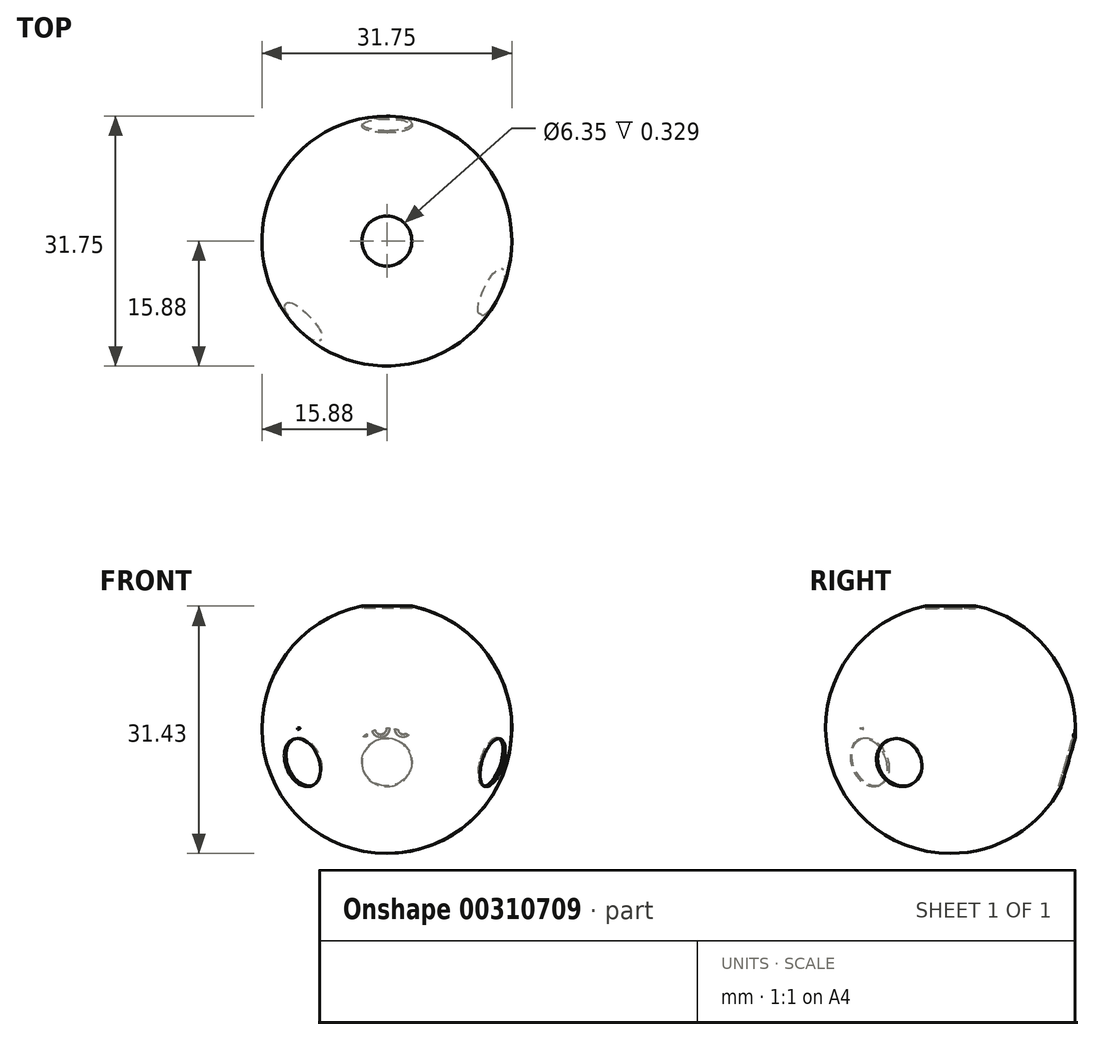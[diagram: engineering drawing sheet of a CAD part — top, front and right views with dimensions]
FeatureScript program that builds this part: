
annotation { "Feature Type Name" : "Feature", "Feature Type Description" : "" }
export const myFeature = defineFeature(function(context is Context, id is Id, definition is map)
    precondition{}
    {
        {
            var Q0;
            Q0=qCreatedBy(makeId("Front.planeOp"),FACE);
            var sketch = newSketch(context, id + "F0", { "sketchPlane" : qUnion([Q0])});
            skArc(sketch, "E0", {"start": v(0, 15.88) * mm, "mid": v(-15.88, 0) * mm, "end": v(0, -15.88) * mm});
            skLineSegment(sketch, "E1", {"start": v(0, 15.88) * mm, "end": v(0, -15.88) * mm});
            skSolve(sketch);
        }
        {
            var Q0;
            Q0=qCreatedBy(makeId("Top.planeOp"),FACE);
            var sketch = newSketch(context, id + "F1", { "sketchPlane" : qUnion([Q0])});
            skCircle(sketch, "E2", {"center": v(0, 0) * mm, "radius": 15.88 * mm});
            skSolve(sketch);
        }
        {
            var Q0;
            Q0=makeQuery(id+"F0.imprint","IMPRINT",FACE,{"disambiguationData":[TD([[makeQuery(id+"F0.imprint","IMPRINT",EDGE,{"derivedFrom":sQuery(id+"F0.wireOp",EDGE,"E0")}),1.0]])]});
            var Q1;
            Q1=sQuery(id+"F1.wireOp",EDGE,"E2");
            revolve(context, id + "F2", {"entities" : qUnion([Q0]), "axis" : qUnion([Q1]), "revolveType" : RevolveType.FULL});
        }
        {
            var Q0;
            Q0=qCreatedBy(makeId("Top.planeOp"),FACE);
            cPlane(context, id + "F3", {"entities" : qUnion([Q0]), "cplaneType" : CPlaneType.OFFSET, "offset" : 15.24 * mm, "width" : 152.4 * mm, "height" : 152.4 * mm});
        }
        {
            var Q0;
            Q0=qCreatedBy(id+"F3.planeOp",FACE);
            cPlane(context, id + "F4", {"entities" : qUnion([Q0]), "cplaneType" : CPlaneType.OFFSET, "offset" : 3 / 203.2 * mm, "oppositeDirection" : true, "width" : 152.4 * mm, "height" : 152.4 * mm});
        }
        {
            var Q0;
            Q0=qCreatedBy(id+"F4.planeOp",FACE);
            var sketch = newSketch(context, id + "F5", { "sketchPlane" : qUnion([Q0])});
            skCircle(sketch, "E3", {"center": v(0, 0) * mm, "radius": 3.18 * mm});
            skSolve(sketch);
        }
        {
            var Q0;
            Q0=qSketchRegion(id+"F5",true);
            extrude(context, id + "F6", {"entities" : qUnion([Q0]), "depth" : 50.8 * mm});
        }
        {
            var Q0;
            Q0=qCreatedBy(makeId("Front.planeOp"),FACE);
            var sketch = newSketch(context, id + "F7", { "sketchPlane" : qUnion([Q0])});
            skLineSegment(sketch, "E4", {"start": v(0, 0) * mm, "end": v(0, -53.82) * mm, "construction": true});
            skLineSegment(sketch, "E5", {"start": v(0, 0) * mm, "end": v(-63.8, 0) * mm, "construction": true});
            skSolve(sketch);
        }
        {
            var Q0;
            Q0=makeQuery(id+"F6.opExtrude","SWEPT_BODY",BODY,{"disambiguationData":[OSD([sQuery(id+"F5.wireOp",EDGE,"E3")])]});
            var Q1;
            Q1=sQuery(id+"F7.wireOp",EDGE,"E5");
            transform(context, id + "F8", {"entities" : qUnion([Q0]), "transformType" : TransformType.ROTATION, "transformAxis" : qUnion([Q1]), "angle" : 106.2 * degree, "makeCopy" : true});
        }
        {
            var Q0;
            Q0=makeQuery(id+"F8.opPattern","COPY",BODY,{"derivedFrom":makeQuery(id+"F6.opExtrude","SWEPT_BODY",BODY,{"disambiguationData":[OSD([sQuery(id+"F5.wireOp",EDGE,"E3")])]}),"instanceName":"1"});
            var Q1;
            Q1=sQuery(id+"F7.wireOp",EDGE,"E4");
            transform(context, id + "F9", {"entities" : qUnion([Q0]), "transformType" : TransformType.ROTATION, "transformAxis" : qUnion([Q1]), "angle" : 115.9 * degree, "makeCopy" : true});
        }
        {
            var Q0;
            Q0=makeQuery(id+"F9.opPattern","COPY",BODY,{"derivedFrom":makeQuery(id+"F8.opPattern","COPY",BODY,{"derivedFrom":makeQuery(id+"F6.opExtrude","SWEPT_BODY",BODY,{"disambiguationData":[OSD([sQuery(id+"F5.wireOp",EDGE,"E3")])]}),"instanceName":"1"}),"instanceName":"1"});
            var Q1;
            Q1=sQuery(id+"F7.wireOp",EDGE,"E4");
            var Q2;
            Q2=sQuery(id+"F7.wireOp",EDGE,"E4");
            transform(context, id + "F10", {"entities" : qUnion([Q0]), "transformType" : TransformType.ROTATION, "transformAxis" : qUnion([Q2]), "angle" : 110 * degree, "makeCopy" : true});
        }
        {
            var Q0;
            Q0=makeQuery(id+"F8.opPattern","COPY",FACE,{"derivedFrom":makeQuery(id+"F6.opExtrude","CAP_FACE",FACE,{"disambiguationData":[OSD([sQuery(id+"F5.wireOp",EDGE,"E3")])],"isStart":false}),"instanceName":"1"});
            cPlane(context, id + "F11", {"entities" : qUnion([Q0]), "cplaneType" : CPlaneType.OFFSET, "offset" : 25.4 * mm, "oppositeDirection" : true, "width" : 152.4 * mm, "height" : 152.4 * mm});
        }
        {
            var Q0;
            Q0=qCreatedBy(id+"F11.planeOp",FACE);
            var sketch = newSketch(context, id + "F12", { "sketchPlane" : qUnion([Q0])});
            skText(sketch, "E6", { "text": "106.2\n", "fontName": "OpenSans-Regular.ttf"});
            const initialGuessF12  = {"E6": [-0.0063, 0.00336, 1, 0, 0.00354]};
            skSetInitialGuess(sketch, initialGuessF12);
            skSolve(sketch);
        }
        {
            var Q0;
            Q0=qSketchRegion(id+"F12",true);
            extrude(context, id + "F13", {"entities" : qUnion([Q0]), "operationType" : NewBodyOperationType.REMOVE, "oppositeDirection" : true, "depth" : 25.4 * mm});
        }
        {
            var Q0;
            Q0=makeQuery(id+"F10.opPattern","COPY",FACE,{"derivedFrom":makeQuery(id+"F9.opPattern","COPY",FACE,{"derivedFrom":makeQuery(id+"F8.opPattern","COPY",FACE,{"derivedFrom":makeQuery(id+"F6.opExtrude","CAP_FACE",FACE,{"disambiguationData":[OSD([sQuery(id+"F5.wireOp",EDGE,"E3")])],"isStart":false}),"instanceName":"1"}),"instanceName":"1"}),"instanceName":"1"});
            cPlane(context, id + "F14", {"entities" : qUnion([Q0]), "cplaneType" : CPlaneType.OFFSET, "offset" : 25.4 * mm, "oppositeDirection" : true, "width" : 152.4 * mm, "height" : 152.4 * mm});
        }
        {
            var Q0;
            Q0=qCreatedBy(id+"F14.planeOp",FACE);
            var sketch = newSketch(context, id + "F15", { "sketchPlane" : qUnion([Q0])});
            skText(sketch, "E7", { "text": "110", "fontName": "OpenSans-Regular.ttf"});
            const initialGuessF15  = {"E7": [-0.00485, 0.00413, 1, 0, 0.00521]};
            skSetInitialGuess(sketch, initialGuessF15);
            skSolve(sketch);
        }
        {
            var Q0;
            Q0=qSketchRegion(id+"F15",true);
            extrude(context, id + "F16", {"entities" : qUnion([Q0]), "operationType" : NewBodyOperationType.REMOVE, "oppositeDirection" : true, "depth" : 25.4 * mm});
        }
        {
            var Q0;
            Q0=makeQuery(id+"F6.opExtrude","SWEPT_BODY",BODY,{"disambiguationData":[OSD([sQuery(id+"F5.wireOp",EDGE,"E3")])]});
            var Q1;
            Q1=makeQuery(id+"F8.opPattern","COPY",BODY,{"derivedFrom":makeQuery(id+"F6.opExtrude","SWEPT_BODY",BODY,{"disambiguationData":[OSD([sQuery(id+"F5.wireOp",EDGE,"E3")])]}),"instanceName":"1"});
            var Q2;
            Q2=makeQuery(id+"F10.opPattern","COPY",BODY,{"derivedFrom":makeQuery(id+"F9.opPattern","COPY",BODY,{"derivedFrom":makeQuery(id+"F8.opPattern","COPY",BODY,{"derivedFrom":makeQuery(id+"F6.opExtrude","SWEPT_BODY",BODY,{"disambiguationData":[OSD([sQuery(id+"F5.wireOp",EDGE,"E3")])]}),"instanceName":"1"}),"instanceName":"1"}),"instanceName":"1"});
            var Q3;
            Q3=makeQuery(id+"F9.opPattern","COPY",BODY,{"derivedFrom":makeQuery(id+"F8.opPattern","COPY",BODY,{"derivedFrom":makeQuery(id+"F6.opExtrude","SWEPT_BODY",BODY,{"disambiguationData":[OSD([sQuery(id+"F5.wireOp",EDGE,"E3")])]}),"instanceName":"1"}),"instanceName":"1"});
            var Q4;
            Q4=makeQuery(id+"F2.opRevolve","SWEPT_BODY",BODY,{"disambiguationData":[OSD([sQuery(id+"F0.wireOp",EDGE,"E0"),sQuery(id+"F0.wireOp",EDGE,"E1")])]});
            booleanBodies(context, id + "F17", {"operationType" : BooleanOperationType.SUBTRACTION, "tools" : qUnion([Q0, Q1, Q2, Q3]), "targets" : qUnion([Q4])});
        }
    });
